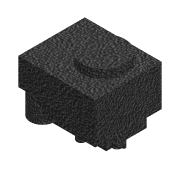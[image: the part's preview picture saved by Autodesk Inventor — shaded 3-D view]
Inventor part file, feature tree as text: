
AUTODESK INVENTOR PART (.ipt)
format: ipt  version: 2022 (Build 260153000, 153)  size: 223,744 bytes
history: native  units: mm
features: extrude x7, sketch x7, projected_geometry x2
ambient origin geometry x8: Origin, YZ Plane, XZ Plane, XY Plane, X Axis, Y Axis, Z Axis, Center Point
bodies: Solid1 (feature_tree)
feature tree (16):
  extrude  "Extrusion1"  Depth=26.4mm
  extrude  "Extrusion2"  Depth=17.0mm
  extrude  "Extrusion3"  Depth=11.5mm
  extrude  "Extrusion4"  Depth=9.6mm
  extrude  "Extrusion5"  Depth=5.5mm TaperAngle=0.0deg
  extrude  "Extrusion6"  Depth=9.6mm TaperAngle=0.0deg
  extrude  "Extrusion7"  Depth=16.0mm
  sketch  "Sketch1"  dims[d0=30.5mm d1=26.4mm]
  sketch  "Sketch2"  dims[d2=16.2mm d3=0.0mm d4=17.0mm]
  sketch  "Sketch3"  dims[d5=11.5mm d6=11.5mm]
  sketch  "Sketch4"  dims[d7=3.5mm d8=0.0mm d9=9.6mm]
  projected_geometry  "Projected Loop1"
  sketch  "Sketch5"  dims[d10=9.6mm d11=5.5mm d12=0.0mm]
  sketch  "Sketch6"  dims[d13=9.6mm d14=9.6mm d15=0.0mm]
  projected_geometry  "Projected Loop2"
  sketch  "Sketch7"  dims[d16=17.0mm d17=16.0mm d18=3.5mm d19=2.5mm d20=2.0mm d21=6.0mm d22=0.0mm d23=3.5mm d24=3.5mm d25=3.5mm d26=3.5mm d27=11.5mm d28=3.0mm d29=9.0mm d30=10.0mm d31=11.5mm d32=6.0mm d33=2.2mm d34=15.5mm d35=1.8mm d36=1.8mm d37=1.8mm d38=6.0mm d39=0.0mm d40=1.3mm d41=1.3mm d42=12.0mm d43=3.0mm d44=4.5mm d45=20.5mm d46=8.7mm d47=0.0mm]
